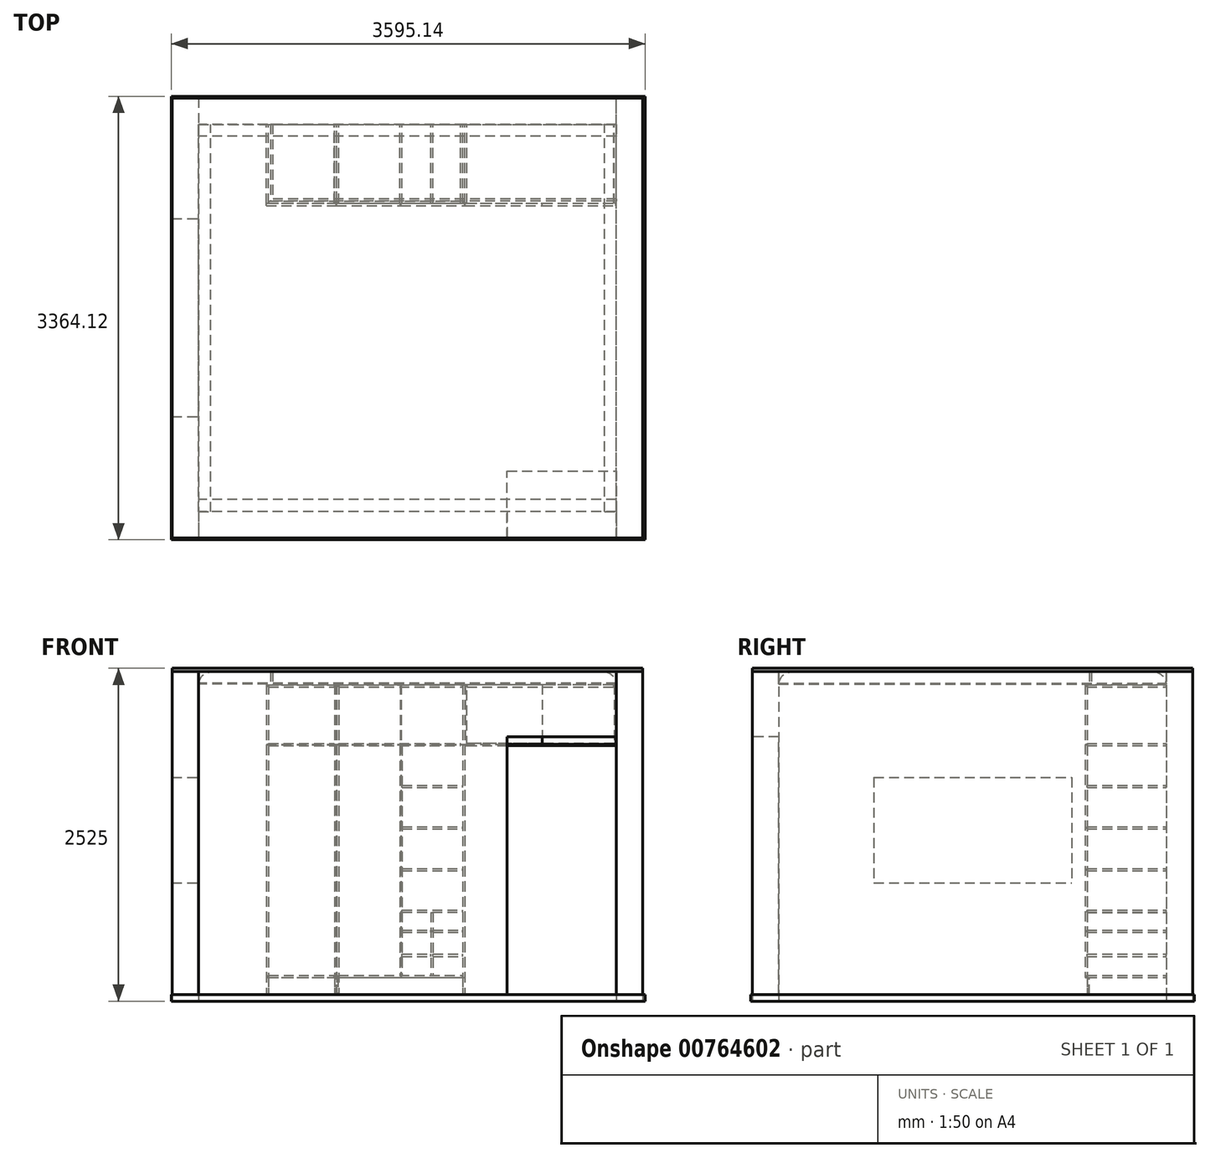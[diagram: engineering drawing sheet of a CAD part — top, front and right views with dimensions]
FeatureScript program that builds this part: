
annotation { "Feature Type Name" : "Feature", "Feature Type Description" : "" }
export const myFeature = defineFeature(function(context is Context, id is Id, definition is map)
    precondition{}
    {
        {
            var Q0;
            Q0=qCreatedBy(makeId("Top.planeOp"),FACE);
            var sketch = newSketch(context, id + "F0", { "sketchPlane" : qUnion([Q0])});
            skLineSegment(sketch, "E0.0.0", {"start": v(-1555, 1015.23) * mm, "end": v(1615, 1015.23) * mm});
            skLineSegment(sketch, "E0.0.1", {"start": v(1615, 1015.23) * mm, "end": v(1615, 1215.23) * mm});
            skLineSegment(sketch, "E0.0.2", {"start": v(1615, 1215.23) * mm, "end": v(-1555, 1215.23) * mm});
            skLineSegment(sketch, "E0.0.3", {"start": v(-1555, 1215.23) * mm, "end": v(-1555, 1015.23) * mm});
            skLineSegment(sketch, "E1.bottom", {"start": v(1815, 1215.23) * mm, "end": v(1615, 1215.23) * mm});
            skLineSegment(sketch, "E1.top", {"start": v(1815, -2124.77) * mm, "end": v(1615, -2124.77) * mm});
            skLineSegment(sketch, "E1.left", {"start": v(1815, 1215.23) * mm, "end": v(1815, -2124.77) * mm});
            skLineSegment(sketch, "E1.right", {"start": v(1615, 1215.23) * mm, "end": v(1615, -2124.77) * mm});
            skLineSegment(sketch, "E2.bottom", {"start": v(-1555, 1215.23) * mm, "end": v(-1755, 1215.23) * mm});
            skLineSegment(sketch, "E2.top", {"start": v(-1555, -2124.77) * mm, "end": v(-1755, -2124.77) * mm});
            skLineSegment(sketch, "E2.left", {"start": v(-1555, 1215.23) * mm, "end": v(-1555, -2124.77) * mm});
            skLineSegment(sketch, "E2.right", {"start": v(-1755, 1215.23) * mm, "end": v(-1755, -2124.77) * mm});
            skLineSegment(sketch, "E3.0.0", {"start": v(-1555, -2124.77) * mm, "end": v(1613.37, -2124.77) * mm});
            skLineSegment(sketch, "E3.0.1", {"start": v(1613.37, -2124.77) * mm, "end": v(1613.37, -1924.77) * mm});
            skLineSegment(sketch, "E3.0.2", {"start": v(1613.37, -1924.77) * mm, "end": v(-1555, -1924.77) * mm});
            skLineSegment(sketch, "E3.0.3", {"start": v(-1555, -1924.77) * mm, "end": v(-1555, -2124.77) * mm});
            skSolve(sketch);
        }
        {
            var Q0;
            {var subQ2=sQuery(id+"F0.wireOp",EDGE,"E1.bottom");Q0=makeQuery(id+"F0.imprint","IMPRINT",FACE,{"disambiguationData":[TD([[makeQuery(id+"F0.imprint","IMPRINT",EDGE,{"derivedFrom":subQ2}),1.0]])]});}
            var Q1;
            {var subQ5=sQuery(id+"F0.wireOp",EDGE,"E2.bottom");Q1=makeQuery(id+"F0.imprint","IMPRINT",FACE,{"disambiguationData":[TD([[makeQuery(id+"F0.imprint","IMPRINT",EDGE,{"derivedFrom":subQ5}),1.0]])]});}
            extrude(context, id + "F1", {"entities" : qUnion([Q0, Q1]), "depth" : 2500 * mm, "offsetDistance" : 25 * mm});
        }
        {
            var Q0;
            {var subQ0=sQuery(id+"F0.wireOp",EDGE,"E0.0.0");Q0=makeQuery(id+"F0.imprint","IMPRINT",FACE,{"disambiguationData":[TD([[makeQuery(id+"F0.imprint","IMPRINT",EDGE,{"derivedFrom":subQ0}),1.0]])]});}
            var Q1;
            Q1=makeQuery(id+"F0.imprint","IMPRINT",FACE,{"disambiguationData":[TD([[makeQuery(id+"F0.imprint","IMPRINT",EDGE,{"derivedFrom":sQuery(id+"F0.wireOp",EDGE,"E3.0.0")}),1.0]])]});
            extrude(context, id + "F2", {"entities" : qUnion([Q0, Q1]), "depth" : 2500 * mm, "offsetDistance" : 25 * mm});
        }
        {
            var Q0;
            Q0=makeQuery(id+"F1.opExtrude","SWEPT_FACE",FACE,{"disambiguationData":[OSD([sQuery(id+"F0.wireOp",EDGE,"E2.left"),sQuery(id+"F0.wireOp",EDGE,"E3.0.3")])]});
            var sketch = newSketch(context, id + "F3", { "sketchPlane" : qUnion([Q0])});
            skLineSegment(sketch, "E4.bottom", {"start": v(-1202.13, 1697) * mm, "end": v(297.87, 1697) * mm});
            skLineSegment(sketch, "E4.top", {"start": v(-1202.13, 897) * mm, "end": v(297.87, 897) * mm});
            skLineSegment(sketch, "E4.left", {"start": v(-1202.13, 1697) * mm, "end": v(-1202.13, 897) * mm});
            skLineSegment(sketch, "E4.right", {"start": v(297.87, 1697) * mm, "end": v(297.87, 897) * mm});
            skSolve(sketch);
        }
        {
            var Q0;
            Q0=makeQuery(id+"F3.imprint","IMPRINT",FACE,{"disambiguationData":[TD([[makeQuery(id+"F3.imprint","IMPRINT",EDGE,{"derivedFrom":sQuery(id+"F3.wireOp",EDGE,"E4.bottom")}),-1.0]])]});
            extrude(context, id + "F4", {"entities" : qUnion([Q0]), "operationType" : NewBodyOperationType.REMOVE, "oppositeDirection" : true, "depth" : 620 * mm, "offsetDistance" : 25 * mm});
        }
        {
            var Q0;
            {var subQ0=sQuery(id+"F0.wireOp",EDGE,"E0.0.0");Q0=makeQuery(id+"F0.imprint","IMPRINT",FACE,{"disambiguationData":[TD([[makeQuery(id+"F0.imprint","IMPRINT",EDGE,{"derivedFrom":subQ0}),1.0]])]});}
            var sketch = newSketch(context, id + "F5", { "sketchPlane" : qUnion([Q0])});
            skLineSegment(sketch, "E5.bottom", {"start": v(-1761.66, -2136.75) * mm, "end": v(1833.48, -2136.75) * mm});
            skLineSegment(sketch, "E5.top", {"start": v(-1761.66, 1227.37) * mm, "end": v(1833.48, 1227.37) * mm});
            skLineSegment(sketch, "E5.left", {"start": v(-1761.66, -2136.75) * mm, "end": v(-1761.66, 1227.37) * mm});
            skLineSegment(sketch, "E5.right", {"start": v(1833.48, -2136.75) * mm, "end": v(1833.48, 1227.37) * mm});
            skSolve(sketch);
        }
        {
            var Q0;
            Q0=makeQuery(id+"F5.imprint","IMPRINT",FACE,{"disambiguationData":[TD([[makeQuery(id+"F5.imprint","IMPRINT",EDGE,{"derivedFrom":sQuery(id+"F5.wireOp",EDGE,"E5.bottom")}),1.0]])]});
            extrude(context, id + "F6", {"entities" : qUnion([Q0]), "depth" : 50 * mm, "offsetDistance" : 25 * mm});
        }
        {
            var Q0;
            Q0=makeQuery(id+"F2.opExtrude","SWEPT_FACE",FACE,{"disambiguationData":[OSD([sQuery(id+"F0.wireOp",EDGE,"E0.0.0")])]});
            var sketch = newSketch(context, id + "F7", { "sketchPlane" : qUnion([Q0])});
            skLineSegment(sketch, "E6.bottom", {"start": v(-1555, 2500) * mm, "end": v(-1462.64, 2500) * mm});
            skLineSegment(sketch, "E6.left", {"start": v(-1555, 2500) * mm, "end": v(-1555, 2412.32) * mm});
            skFitSpline(sketch, "E7", {"points": [v(-1555, 2400.43) * mm, v(-1455, 2500) * mm], "startDerivative": vector(33.84, 289.83) * mm, "endDerivative": vector(27.08, 13.3) * mm});
            skArc(sketch, "E8.filletArc", {"start": v(-1555, 2412.32) * mm, "mid": v(-1554.18, 2411.42) * mm, "end": v(-1553.22, 2412.15) * mm});
            skArc(sketch, "E9.filletArc", {"start": v(-1462.48, 2498.21) * mm, "mid": v(-1461.75, 2499.18) * mm, "end": v(-1462.64, 2500) * mm});
            skLineSegment(sketch, "E10.bottom", {"start": v(1615, 2500) * mm, "end": v(1615, 2407.64) * mm});
            skLineSegment(sketch, "E10.left", {"start": v(1615, 2500) * mm, "end": v(1527.32, 2500) * mm});
            skFitSpline(sketch, "E11", {"points": [v(1515.43, 2500) * mm, v(1615, 2400) * mm], "startDerivative": vector(289.83, -33.84) * mm, "endDerivative": vector(13.3, -27.08) * mm});
            skArc(sketch, "E12.filletArc", {"start": v(1527.32, 2500) * mm, "mid": v(1526.42, 2499.18) * mm, "end": v(1527.15, 2498.22) * mm});
            skArc(sketch, "E13.filletArc", {"start": v(1613.22, 2407.48) * mm, "mid": v(1614.18, 2406.75) * mm, "end": v(1615, 2407.64) * mm});
            skSolve(sketch);
        }
        {
            var Q0;
            Q0=qSketchRegion(id+"F7",true);
            extrude(context, id + "F8", {"entities" : qUnion([Q0]), "depth" : 2940 * mm, "offsetDistance" : 25 * mm});
        }
        {
            var Q0;
            Q0=makeQuery(id+"F1.opExtrude","SWEPT_FACE",FACE,{"disambiguationData":[OSD([sQuery(id+"F0.wireOp",EDGE,"E2.left"),sQuery(id+"F0.wireOp",EDGE,"E3.0.3")])]});
            var sketch = newSketch(context, id + "F9", { "sketchPlane" : qUnion([Q0])});
            skLineSegment(sketch, "E14.bottom", {"start": v(-1924.58, 2500) * mm, "end": v(-1832.23, 2500) * mm});
            skLineSegment(sketch, "E14.left", {"start": v(-1924.58, 2500) * mm, "end": v(-1924.58, 2412.32) * mm});
            skFitSpline(sketch, "E15", {"points": [v(-1924.58, 2400.43) * mm, v(-1824.58, 2500) * mm], "startDerivative": vector(33.84, 289.83) * mm, "endDerivative": vector(27.08, 13.3) * mm});
            skArc(sketch, "E16.filletArc", {"start": v(-1924.58, 2412.32) * mm, "mid": v(-1923.77, 2411.43) * mm, "end": v(-1922.8, 2412.15) * mm});
            skArc(sketch, "E17.filletArc", {"start": v(-1832.06, 2498.22) * mm, "mid": v(-1831.33, 2499.19) * mm, "end": v(-1832.23, 2500) * mm});
            skLineSegment(sketch, "E18.bottom", {"start": v(1014.88, 2500) * mm, "end": v(1014.88, 2407.64) * mm});
            skLineSegment(sketch, "E18.left", {"start": v(1014.88, 2500) * mm, "end": v(927.2, 2500) * mm});
            skFitSpline(sketch, "E19", {"points": [v(915.3, 2500) * mm, v(1014.88, 2400) * mm], "startDerivative": vector(289.83, -33.84) * mm, "endDerivative": vector(13.3, -27.08) * mm});
            skArc(sketch, "E20.filletArc", {"start": v(927.2, 2500) * mm, "mid": v(926.3, 2499.18) * mm, "end": v(927.03, 2498.22) * mm});
            skArc(sketch, "E21.filletArc", {"start": v(1013.1, 2407.48) * mm, "mid": v(1014.06, 2406.75) * mm, "end": v(1014.88, 2407.64) * mm});
            skSolve(sketch);
        }
        {
            var Q0;
            Q0=qSketchRegion(id+"F9",true);
            extrude(context, id + "F10", {"entities" : qUnion([Q0]), "depth" : 3169.2 * mm, "offsetDistance" : 25 * mm});
        }
        {
            var Q0;
            Q0=makeQuery(id+"F2.opExtrude","SWEPT_FACE",FACE,{"disambiguationData":[OSD([sQuery(id+"F0.wireOp",EDGE,"E3.0.0")])]});
            var sketch = newSketch(context, id + "F11", { "sketchPlane" : qUnion([Q0])});
            skLineSegment(sketch, "E22.bottom", {"start": v(1613.37, 49.92) * mm, "end": v(785.99, 49.92) * mm});
            skLineSegment(sketch, "E22.top", {"start": v(1613.37, 2005.08) * mm, "end": v(785.99, 2005.08) * mm});
            skLineSegment(sketch, "E22.left", {"start": v(1613.37, 49.92) * mm, "end": v(1613.37, 2005.08) * mm});
            skLineSegment(sketch, "E22.right", {"start": v(785.99, 49.92) * mm, "end": v(785.99, 2005.08) * mm});
            skSolve(sketch);
        }
        {
            var Q0;
            Q0=makeQuery(id+"F11.imprint","IMPRINT",FACE,{"disambiguationData":[TD([[makeQuery(id+"F11.imprint","IMPRINT",EDGE,{"derivedFrom":sQuery(id+"F11.wireOp",EDGE,"E22.bottom")}),-1.0]])]});
            extrude(context, id + "F12", {"entities" : qUnion([Q0]), "operationType" : NewBodyOperationType.REMOVE, "oppositeDirection" : true, "depth" : 510 * mm, "offsetDistance" : 25 * mm});
        }
        {
            var Q0;
            Q0=makeQuery(id+"F2.opExtrude","CAP_FACE",FACE,{"disambiguationData":[OSD([sQuery(id+"F0.wireOp",EDGE,"E0.0.0"),sQuery(id+"F0.wireOp",EDGE,"E0.0.2"),sQuery(id+"F0.wireOp",EDGE,"E1.right"),sQuery(id+"F0.wireOp",EDGE,"E2.left")])],"isStart":false});
            var sketch = newSketch(context, id + "F13", { "sketchPlane" : qUnion([Q0])});
            skLineSegment(sketch, "E23.0", {"start": v(1815, 1215.23) * mm, "end": v(-1755, 1215.23) * mm});
            skLineSegment(sketch, "E24.0", {"start": v(1815, 1215.23) * mm, "end": v(1815, -2124.77) * mm});
            skLineSegment(sketch, "E25.0", {"start": v(-1755, -2124.77) * mm, "end": v(1815, -2124.77) * mm});
            skLineSegment(sketch, "E26.0", {"start": v(-1755, 1215.23) * mm, "end": v(-1755, -2124.77) * mm});
            skSolve(sketch);
        }
        {
            var Q0;
            Q0=qSketchRegion(id+"F13",true);
            extrude(context, id + "F14", {"entities" : qUnion([Q0]), "depth" : 25 * mm, "offsetDistance" : 25 * mm});
        }
        {
            var Q0;
            Q0=makeQuery(id+"F2.opExtrude","SWEPT_FACE",FACE,{"disambiguationData":[OSD([sQuery(id+"F0.wireOp",EDGE,"E0.0.0")])]});
            var sketch = newSketch(context, id + "F15", { "sketchPlane" : qUnion([Q0])});
            skLineSegment(sketch, "E27", {"start": v(498.7, 98.2) * mm, "end": v(1598.7, 98.2) * mm});
            skLineSegment(sketch, "E28", {"start": v(-930.04, 98.4) * mm, "end": v(469.96, 98.4) * mm});
            skLineSegment(sketch, "E29", {"start": v(-930.56, 51.34) * mm, "end": v(-930.04, 1954.15) * mm});
            skLineSegment(sketch, "E30", {"start": v(-930.04, 1954.15) * mm, "end": v(-930.04, 2500) * mm});
            skSolve(sketch);
        }
        {
            var Q0;
            {var subQ0=sQuery(id+"F0.wireOp",EDGE,"E0.0.0");Q0=makeQuery(id+"F15.imprint","IMPRINT",FACE,{"disambiguationData":[TD([[makeQuery(id+"F15.imprint","IMPRINT",EDGE,{"derivedFrom":makeQuery(id+"F2.opExtrude","CAP_EDGE",EDGE,{"disambiguationData":[OSD([subQ0])],"isStart":true})}),1.0]])]});}
            var sketch = newSketch(context, id + "F16", { "sketchPlane" : qUnion([Q0])});
            skLineSegment(sketch, "E31.bottom", {"start": v(-1039.66, 2400.3) * mm, "end": v(-1023.66, 2400.3) * mm});
            skLineSegment(sketch, "E31.top", {"start": v(-1039.66, 50.3) * mm, "end": v(-1023.66, 50.3) * mm});
            skLineSegment(sketch, "E31.left", {"start": v(-1039.66, 2400.3) * mm, "end": v(-1039.66, 50.3) * mm});
            skLineSegment(sketch, "E31.right", {"start": v(-1023.66, 2400.3) * mm, "end": v(-1023.66, 50.3) * mm});
            skLineSegment(sketch, "E32.bottom", {"start": v(450, 2400.3) * mm, "end": v(466, 2400.3) * mm});
            skLineSegment(sketch, "E32.top", {"start": v(450, 50.3) * mm, "end": v(466, 50.3) * mm});
            skLineSegment(sketch, "E32.left", {"start": v(450, 2400.3) * mm, "end": v(450, 50.3) * mm});
            skLineSegment(sketch, "E32.right", {"start": v(466, 2400.3) * mm, "end": v(466, 50.3) * mm});
            skLineSegment(sketch, "E33.bottom", {"start": v(-1023.54, 1937.99) * mm, "end": v(-1023.54, 1953.99) * mm});
            skLineSegment(sketch, "E33.top", {"start": v(-524.4, 1937.99) * mm, "end": v(-524.4, 1953.99) * mm});
            skLineSegment(sketch, "E33.left", {"start": v(-1023.54, 1937.99) * mm, "end": v(-524.4, 1937.99) * mm});
            skLineSegment(sketch, "E33.right", {"start": v(-1023.54, 1953.99) * mm, "end": v(-524.4, 1953.99) * mm});
            skLineSegment(sketch, "E34.bottom", {"start": v(-1023.33, 2384.28) * mm, "end": v(-1023.33, 2400.28) * mm});
            skLineSegment(sketch, "E34.top", {"start": v(-524.01, 2384.28) * mm, "end": v(-524.01, 2400.28) * mm});
            skLineSegment(sketch, "E34.left", {"start": v(-1023.33, 2384.28) * mm, "end": v(-524.01, 2384.28) * mm});
            skLineSegment(sketch, "E34.right", {"start": v(-1023.33, 2400.28) * mm, "end": v(-524.01, 2400.28) * mm});
            skLineSegment(sketch, "E35.bottom", {"start": v(-1023.48, 180.4) * mm, "end": v(-1023.48, 196.4) * mm});
            skLineSegment(sketch, "E35.top", {"start": v(-524.51, 180.4) * mm, "end": v(-524.51, 196.4) * mm});
            skLineSegment(sketch, "E35.left", {"start": v(-1023.48, 180.4) * mm, "end": v(-524.51, 180.4) * mm});
            skLineSegment(sketch, "E35.right", {"start": v(-1023.48, 196.4) * mm, "end": v(-524.51, 196.4) * mm});
            skLineSegment(sketch, "E36.bottom", {"start": v(-523.66, 2400.3) * mm, "end": v(-507.66, 2400.3) * mm});
            skLineSegment(sketch, "E36.top", {"start": v(-523.66, 50.3) * mm, "end": v(-507.66, 50.3) * mm});
            skLineSegment(sketch, "E36.left", {"start": v(-523.66, 2400.3) * mm, "end": v(-523.66, 50.3) * mm});
            skLineSegment(sketch, "E36.right", {"start": v(-507.66, 2400.3) * mm, "end": v(-507.66, 50.3) * mm});
            skLineSegment(sketch, "E37.bottom", {"start": v(-28.8, 1937.8) * mm, "end": v(-12.8, 1937.8) * mm});
            skLineSegment(sketch, "E37.top", {"start": v(-28.8, 196.92) * mm, "end": v(-12.8, 196.92) * mm});
            skLineSegment(sketch, "E37.left", {"start": v(-28.8, 1937.8) * mm, "end": v(-28.8, 196.92) * mm});
            skLineSegment(sketch, "E37.right", {"start": v(-12.8, 1937.8) * mm, "end": v(-12.8, 196.92) * mm});
            skLineSegment(sketch, "E38.bottom", {"start": v(-491.17, 2384.3) * mm, "end": v(-491.17, 2400.3) * mm});
            skLineSegment(sketch, "E38.top", {"start": v(449.95, 2384.3) * mm, "end": v(449.95, 2400.3) * mm});
            skLineSegment(sketch, "E38.left", {"start": v(-491.17, 2384.3) * mm, "end": v(449.95, 2384.3) * mm});
            skLineSegment(sketch, "E38.right", {"start": v(-491.17, 2400.3) * mm, "end": v(449.95, 2400.3) * mm});
            skLineSegment(sketch, "E39.bottom", {"start": v(-491.28, 1937.98) * mm, "end": v(-491.28, 1953.98) * mm});
            skLineSegment(sketch, "E39.top", {"start": v(433.7, 1937.98) * mm, "end": v(433.7, 1953.98) * mm});
            skLineSegment(sketch, "E39.left", {"start": v(-491.28, 1937.98) * mm, "end": v(433.7, 1937.98) * mm});
            skLineSegment(sketch, "E39.right", {"start": v(-491.28, 1953.98) * mm, "end": v(433.7, 1953.98) * mm});
            skLineSegment(sketch, "E40.bottom", {"start": v(-491.2, 180.4) * mm, "end": v(-491.2, 196.4) * mm});
            skLineSegment(sketch, "E40.top", {"start": v(449.77, 180.4) * mm, "end": v(449.77, 196.4) * mm});
            skLineSegment(sketch, "E40.left", {"start": v(-491.2, 180.4) * mm, "end": v(449.77, 180.4) * mm});
            skLineSegment(sketch, "E40.right", {"start": v(-491.2, 196.4) * mm, "end": v(449.77, 196.4) * mm});
            skPoint(sketch, "E41", {"position": v(-28.8, 1937.98) * mm});
            skLineSegment(sketch, "E42.bottom", {"start": v(-11.33, 1621.98) * mm, "end": v(-11.33, 1637.98) * mm});
            skLineSegment(sketch, "E42.top", {"start": v(449.6, 1621.98) * mm, "end": v(449.6, 1637.98) * mm});
            skLineSegment(sketch, "E42.left", {"start": v(-11.33, 1621.98) * mm, "end": v(449.6, 1621.98) * mm});
            skLineSegment(sketch, "E42.right", {"start": v(-11.33, 1637.98) * mm, "end": v(449.6, 1637.98) * mm});
            skLineSegment(sketch, "E43.bottom", {"start": v(-11.33, 1305.98) * mm, "end": v(-11.33, 1321.98) * mm});
            skLineSegment(sketch, "E43.top", {"start": v(449.6, 1305.98) * mm, "end": v(449.6, 1321.98) * mm});
            skLineSegment(sketch, "E43.left", {"start": v(-11.33, 1305.98) * mm, "end": v(449.6, 1305.98) * mm});
            skLineSegment(sketch, "E43.right", {"start": v(-11.33, 1321.98) * mm, "end": v(449.6, 1321.98) * mm});
            skLineSegment(sketch, "E44.bottom", {"start": v(-11.33, 989.98) * mm, "end": v(-11.33, 1005.98) * mm});
            skLineSegment(sketch, "E44.top", {"start": v(449.6, 989.98) * mm, "end": v(449.6, 1005.98) * mm});
            skLineSegment(sketch, "E44.left", {"start": v(-11.33, 989.98) * mm, "end": v(449.6, 989.98) * mm});
            skLineSegment(sketch, "E44.right", {"start": v(-11.33, 1005.98) * mm, "end": v(449.6, 1005.98) * mm});
            skLineSegment(sketch, "E45.bottom", {"start": v(-11.33, 673.98) * mm, "end": v(-11.33, 689.98) * mm});
            skLineSegment(sketch, "E45.top", {"start": v(449.6, 673.98) * mm, "end": v(449.6, 689.98) * mm});
            skLineSegment(sketch, "E45.left", {"start": v(-11.33, 673.98) * mm, "end": v(449.6, 673.98) * mm});
            skLineSegment(sketch, "E45.right", {"start": v(-11.33, 689.98) * mm, "end": v(449.6, 689.98) * mm});
            skLineSegment(sketch, "E46.top", {"start": v(207.2, 196.51) * mm, "end": v(223.2, 196.51) * mm});
            skLineSegment(sketch, "E46.left", {"start": v(207.2, 672.57) * mm, "end": v(207.2, 196.51) * mm});
            skLineSegment(sketch, "E46.right", {"start": v(223.2, 672.57) * mm, "end": v(223.2, 196.51) * mm});
            skLineSegment(sketch, "E47", {"start": v(207.2, 672.57) * mm, "end": v(223.2, 672.57) * mm});
            skLineSegment(sketch, "E48.bottom", {"start": v(-11.33, 523.98) * mm, "end": v(-11.33, 539.98) * mm});
            skLineSegment(sketch, "E48.top", {"start": v(206.59, 523.98) * mm, "end": v(206.59, 539.98) * mm});
            skLineSegment(sketch, "E48.left", {"start": v(-11.33, 523.98) * mm, "end": v(206.59, 523.98) * mm});
            skLineSegment(sketch, "E48.right", {"start": v(-11.33, 539.98) * mm, "end": v(206.59, 539.98) * mm});
            skLineSegment(sketch, "E49.bottom", {"start": v(-11.33, 339.98) * mm, "end": v(-11.33, 355.98) * mm});
            skLineSegment(sketch, "E49.top", {"start": v(206.59, 339.98) * mm, "end": v(206.59, 355.98) * mm});
            skLineSegment(sketch, "E49.left", {"start": v(-11.33, 339.98) * mm, "end": v(206.59, 339.98) * mm});
            skLineSegment(sketch, "E49.right", {"start": v(-11.33, 355.98) * mm, "end": v(206.59, 355.98) * mm});
            skLineSegment(sketch, "E50.bottom", {"start": v(223.6, 523.98) * mm, "end": v(223.6, 539.98) * mm});
            skLineSegment(sketch, "E50.top", {"start": v(449.5, 523.98) * mm, "end": v(449.5, 539.98) * mm});
            skLineSegment(sketch, "E50.left", {"start": v(223.6, 523.98) * mm, "end": v(449.5, 523.98) * mm});
            skLineSegment(sketch, "E50.right", {"start": v(223.6, 539.98) * mm, "end": v(449.5, 539.98) * mm});
            skLineSegment(sketch, "E51.bottom", {"start": v(223.6, 339.98) * mm, "end": v(223.6, 355.98) * mm});
            skLineSegment(sketch, "E51.top", {"start": v(449.82, 339.98) * mm, "end": v(449.82, 355.98) * mm});
            skLineSegment(sketch, "E51.left", {"start": v(223.6, 339.98) * mm, "end": v(449.82, 339.98) * mm});
            skLineSegment(sketch, "E51.right", {"start": v(223.6, 355.98) * mm, "end": v(449.82, 355.98) * mm});
            skLineSegment(sketch, "E52.bottom", {"start": v(-507.52, 2400.3) * mm, "end": v(-491.52, 2400.3) * mm});
            skLineSegment(sketch, "E52.top", {"start": v(-507.52, 50.3) * mm, "end": v(-491.52, 50.3) * mm});
            skLineSegment(sketch, "E52.left", {"start": v(-507.52, 2400.3) * mm, "end": v(-507.52, 50.3) * mm});
            skLineSegment(sketch, "E52.right", {"start": v(-491.52, 2400.3) * mm, "end": v(-491.52, 50.3) * mm});
            skSolve(sketch);
        }
        {
            var Q0;
            Q0=makeQuery(id+"F16.imprint","IMPRINT",FACE,{"disambiguationData":[TD([[makeQuery(id+"F16.imprint","IMPRINT",EDGE,{"derivedFrom":sQuery(id+"F16.wireOp",EDGE,"E32.bottom")}),-1.0]])]});
            var Q1;
            {var subQ1=sQuery(id+"F16.wireOp",EDGE,"E31.bottom");Q1=makeQuery(id+"F16.imprint","IMPRINT",FACE,{"disambiguationData":[TD([[makeQuery(id+"F16.imprint","IMPRINT",EDGE,{"derivedFrom":subQ1}),-1.0]])]});}
            var Q2;
            Q2=makeQuery(id+"F16.imprint","IMPRINT",FACE,{"disambiguationData":[TD([[makeQuery(id+"F16.imprint","IMPRINT",EDGE,{"derivedFrom":sQuery(id+"F16.wireOp",EDGE,"E34.bottom")}),-1.0]])]});
            var Q3;
            Q3=makeQuery(id+"F16.imprint","IMPRINT",FACE,{"disambiguationData":[TD([[makeQuery(id+"F16.imprint","IMPRINT",EDGE,{"derivedFrom":sQuery(id+"F16.wireOp",EDGE,"E36.bottom")}),-1.0]])]});
            var Q4;
            Q4=makeQuery(id+"F16.imprint","IMPRINT",FACE,{"disambiguationData":[TD([[makeQuery(id+"F16.imprint","IMPRINT",EDGE,{"derivedFrom":sQuery(id+"F16.wireOp",EDGE,"E35.bottom")}),-1.0]])]});
            var Q5;
            Q5=makeQuery(id+"F16.imprint","IMPRINT",FACE,{"disambiguationData":[TD([[makeQuery(id+"F16.imprint","IMPRINT",EDGE,{"derivedFrom":sQuery(id+"F16.wireOp",EDGE,"E38.bottom")}),-1.0]])]});
            var Q6;
            Q6=makeQuery(id+"F16.imprint","IMPRINT",FACE,{"disambiguationData":[TD([[makeQuery(id+"F16.imprint","IMPRINT",EDGE,{"derivedFrom":sQuery(id+"F16.wireOp",EDGE,"E40.bottom")}),-1.0]])]});
            var Q7;
            Q7=makeQuery(id+"F16.imprint","IMPRINT",FACE,{"disambiguationData":[TD([[makeQuery(id+"F16.imprint","IMPRINT",EDGE,{"derivedFrom":sQuery(id+"F16.wireOp",EDGE,"E37.bottom")}),-1.0]])]});
            var Q8;
            Q8=makeQuery(id+"F16.imprint","IMPRINT",FACE,{"disambiguationData":[TD([[makeQuery(id+"F16.imprint","IMPRINT",EDGE,{"derivedFrom":sQuery(id+"F16.wireOp",EDGE,"E52.bottom")}),-1.0]])]});
            extrude(context, id + "F17", {"entities" : qUnion([Q0, Q1, Q2, Q3, Q4, Q5, Q6, Q7, Q8]), "depth" : 600 * mm, "offsetDistance" : 25 * mm});
        }
        {
            var Q0;
            Q0=makeQuery(id+"F16.imprint","IMPRINT",FACE,{"disambiguationData":[TD([[makeQuery(id+"F16.imprint","IMPRINT",EDGE,{"derivedFrom":sQuery(id+"F16.wireOp",EDGE,"E33.bottom")}),-1.0]])]});
            var Q1;
            Q1=makeQuery(id+"F16.imprint","IMPRINT",FACE,{"disambiguationData":[TD([[makeQuery(id+"F16.imprint","IMPRINT",EDGE,{"derivedFrom":sQuery(id+"F16.wireOp",EDGE,"E39.bottom")}),-1.0]])]});
            var Q2;
            Q2=makeQuery(id+"F16.imprint","IMPRINT",FACE,{"disambiguationData":[TD([[makeQuery(id+"F16.imprint","IMPRINT",EDGE,{"derivedFrom":sQuery(id+"F16.wireOp",EDGE,"E42.bottom")}),-1.0]])]});
            var Q3;
            Q3=makeQuery(id+"F16.imprint","IMPRINT",FACE,{"disambiguationData":[TD([[makeQuery(id+"F16.imprint","IMPRINT",EDGE,{"derivedFrom":sQuery(id+"F16.wireOp",EDGE,"E43.bottom")}),-1.0]])]});
            var Q4;
            Q4=makeQuery(id+"F16.imprint","IMPRINT",FACE,{"disambiguationData":[TD([[makeQuery(id+"F16.imprint","IMPRINT",EDGE,{"derivedFrom":sQuery(id+"F16.wireOp",EDGE,"E44.bottom")}),-1.0]])]});
            var Q5;
            Q5=makeQuery(id+"F16.imprint","IMPRINT",FACE,{"disambiguationData":[TD([[makeQuery(id+"F16.imprint","IMPRINT",EDGE,{"derivedFrom":sQuery(id+"F16.wireOp",EDGE,"E45.bottom")}),-1.0]])]});
            var Q6;
            Q6=makeQuery(id+"F16.imprint","IMPRINT",FACE,{"disambiguationData":[TD([[makeQuery(id+"F16.imprint","IMPRINT",EDGE,{"derivedFrom":sQuery(id+"F16.wireOp",EDGE,"E46.top")}),1.0]])]});
            var Q7;
            Q7=makeQuery(id+"F16.imprint","IMPRINT",FACE,{"disambiguationData":[TD([[makeQuery(id+"F16.imprint","IMPRINT",EDGE,{"derivedFrom":sQuery(id+"F16.wireOp",EDGE,"E48.bottom")}),-1.0]])]});
            var Q8;
            Q8=makeQuery(id+"F16.imprint","IMPRINT",FACE,{"disambiguationData":[TD([[makeQuery(id+"F16.imprint","IMPRINT",EDGE,{"derivedFrom":sQuery(id+"F16.wireOp",EDGE,"E49.bottom")}),-1.0]])]});
            var Q9;
            Q9=makeQuery(id+"F16.imprint","IMPRINT",FACE,{"disambiguationData":[TD([[makeQuery(id+"F16.imprint","IMPRINT",EDGE,{"derivedFrom":sQuery(id+"F16.wireOp",EDGE,"E50.bottom")}),-1.0]])]});
            var Q10;
            Q10=makeQuery(id+"F16.imprint","IMPRINT",FACE,{"disambiguationData":[TD([[makeQuery(id+"F16.imprint","IMPRINT",EDGE,{"derivedFrom":sQuery(id+"F16.wireOp",EDGE,"E51.bottom")}),-1.0]])]});
            extrude(context, id + "F18", {"entities" : qUnion([Q0, Q1, Q2, Q3, Q4, Q5, Q6, Q7, Q8, Q9, Q10]), "depth" : 600 * mm, "offsetDistance" : 25 * mm});
        }
        {
            var Q0;
            Q0=makeQuery(id+"F16.imprint","IMPRINT",FACE,{"disambiguationData":[TD([[makeQuery(id+"F16.imprint","IMPRINT",EDGE,{"derivedFrom":sQuery(id+"F16.wireOp",EDGE,"E31.bottom")}),1.0]])]});
            var sketch = newSketch(context, id + "F19", { "sketchPlane" : qUnion([Q0])});
            skLineSegment(sketch, "E53.0.0", {"start": v(482.33, 2384.3) * mm, "end": v(1596.28, 2384.3) * mm});
            skLineSegment(sketch, "E53.0.1", {"start": v(1596.28, 2384.3) * mm, "end": v(1596.28, 2400.3) * mm});
            skLineSegment(sketch, "E53.0.2", {"start": v(1596.28, 2400.3) * mm, "end": v(482.33, 2400.3) * mm});
            skLineSegment(sketch, "E53.0.3", {"start": v(482.33, 2400.3) * mm, "end": v(482.33, 2384.3) * mm});
            skLineSegment(sketch, "E54.0.0", {"start": v(466.1, 2400.3) * mm, "end": v(466.1, 1937.9) * mm});
            skLineSegment(sketch, "E54.0.1", {"start": v(466.1, 1937.9) * mm, "end": v(482.1, 1937.9) * mm});
            skLineSegment(sketch, "E54.0.2", {"start": v(482.1, 1937.9) * mm, "end": v(482.1, 2400.3) * mm});
            skLineSegment(sketch, "E54.0.3", {"start": v(482.1, 2400.3) * mm, "end": v(466.1, 2400.3) * mm});
            skLineSegment(sketch, "E55.0.0", {"start": v(1597.76, 2400.3) * mm, "end": v(1597.76, 1937.95) * mm});
            skLineSegment(sketch, "E55.0.1", {"start": v(1597.76, 1937.95) * mm, "end": v(1613.76, 1937.95) * mm});
            skLineSegment(sketch, "E55.0.2", {"start": v(1613.76, 1937.95) * mm, "end": v(1613.76, 2400.3) * mm});
            skLineSegment(sketch, "E55.0.3", {"start": v(1613.76, 2400.3) * mm, "end": v(1597.76, 2400.3) * mm});
            skLineSegment(sketch, "E56.0.0", {"start": v(482.28, 1937.98) * mm, "end": v(1597.13, 1937.98) * mm});
            skLineSegment(sketch, "E56.0.1", {"start": v(1597.13, 1937.98) * mm, "end": v(1597.13, 1953.98) * mm});
            skLineSegment(sketch, "E56.0.2", {"start": v(1597.13, 1953.98) * mm, "end": v(482.28, 1953.98) * mm});
            skLineSegment(sketch, "E56.0.3", {"start": v(482.28, 1953.98) * mm, "end": v(482.28, 1937.98) * mm});
            skSolve(sketch);
        }
        {
            var Q0;
            Q0=qSketchRegion(id+"F19",true);
            extrude(context, id + "F20", {"entities" : qUnion([Q0]), "depth" : 600 * mm, "offsetDistance" : 25 * mm});
        }
        {
            var Q0;
            Q0=makeQuery(id+"F17.opExtrude","SWEPT_FACE",FACE,{"disambiguationData":[OSD([sQuery(id+"F16.wireOp",EDGE,"E36.left")])]});
            var sketch = newSketch(context, id + "F21", { "sketchPlane" : qUnion([Q0])});
            skLineSegment(sketch, "E57.bottom", {"start": v(-431.22, 180.59) * mm, "end": v(-415.22, 180.59) * mm});
            skLineSegment(sketch, "E57.top", {"start": v(-431.22, 49.78) * mm, "end": v(-415.22, 49.78) * mm});
            skLineSegment(sketch, "E57.left", {"start": v(-431.22, 180.59) * mm, "end": v(-431.22, 49.78) * mm});
            skLineSegment(sketch, "E57.right", {"start": v(-415.22, 180.59) * mm, "end": v(-415.22, 49.78) * mm});
            skSolve(sketch);
        }
        {
            var Q0;
            {var subQ0=sQuery(id+"F21.wireOp",EDGE,"E57.left");var subQ1=sQuery(id+"F21.wireOp",EDGE,"E57.bottom");var subQ2=makeQuery(id+"F21.imprint","INTERSECT",VERTEX,{"derivedFrom":[subQ1,subQ0]});Q0=makeQuery(id+"F21.imprint","IMPRINT",FACE,{"disambiguationData":[TD([[makeQuery(id+"F21.imprint","IMPRINT",EDGE,{"disambiguationData":[TD([[subQ2,-1.0]])],"derivedFrom":subQ1}),-1.0]])]});}
            extrude(context, id + "F22", {"entities" : qUnion([Q0]), "operationType" : NewBodyOperationType.REMOVE, "oppositeDirection" : true, "depth" : 25 * mm, "offsetDistance" : 25 * mm});
        }
        {
            var Q0;
            {var subQ0=sQuery(id+"F21.wireOp",EDGE,"E57.left");var subQ1=sQuery(id+"F21.wireOp",EDGE,"E57.bottom");var subQ2=makeQuery(id+"F21.imprint","INTERSECT",VERTEX,{"derivedFrom":[subQ1,subQ0]});Q0=makeQuery(id+"F21.imprint","IMPRINT",FACE,{"disambiguationData":[TD([[makeQuery(id+"F21.imprint","IMPRINT",EDGE,{"disambiguationData":[TD([[subQ2,-1.0]])],"derivedFrom":subQ1}),-1.0]])]});}
            extrude(context, id + "F23", {"entities" : qUnion([Q0]), "depth" : 499.9 * mm, "offsetDistance" : 25 * mm, "hasSecondDirection" : true, "secondDirectionOppositeDirection" : true, "secondDirectionDepth" : 974 * mm});
        }
        {
            var Q0;
            Q0=makeQuery(id+"F17.opExtrude","CAP_FACE",FACE,{"disambiguationData":[OSD([sQuery(id+"F16.wireOp",EDGE,"E31.bottom"),sQuery(id+"F16.wireOp",EDGE,"E31.top"),sQuery(id+"F16.wireOp",EDGE,"E31.left"),sQuery(id+"F16.wireOp",EDGE,"E31.right")])],"isStart":false});
            var sketch = newSketch(context, id + "F24", { "sketchPlane" : qUnion([Q0])});
            skLineSegment(sketch, "E58.0", {"start": v(-1039.66, 1945.74) * mm, "end": v(-510.25, 1945.9) * mm});
            skLineSegment(sketch, "E59.0", {"start": v(-1039.66, 180.25) * mm, "end": v(-510.25, 180.58) * mm});
            skLineSegment(sketch, "E60.0", {"start": v(-510.25, 1945.9) * mm, "end": v(-510.25, 180.58) * mm});
            skLineSegment(sketch, "E61.0", {"start": v(-1039.66, 1945.74) * mm, "end": v(-1039.66, 180.25) * mm});
            skLineSegment(sketch, "E62.0", {"start": v(-507.65, 1945.9) * mm, "end": v(-22.65, 1945.89) * mm});
            skLineSegment(sketch, "E63.0", {"start": v(-507.65, 180.6) * mm, "end": v(-22.65, 180.9) * mm});
            skLineSegment(sketch, "E64.0", {"start": v(-22.65, 1945.89) * mm, "end": v(-22.65, 180.9) * mm});
            skLineSegment(sketch, "E65.0", {"start": v(-507.65, 1945.9) * mm, "end": v(-507.65, 180.6) * mm});
            skLineSegment(sketch, "E66.0", {"start": v(-19.04, 1945.87) * mm, "end": v(465.95, 1945.86) * mm});
            skLineSegment(sketch, "E67.0", {"start": v(-19.04, 180.56) * mm, "end": v(465.95, 180.87) * mm});
            skLineSegment(sketch, "E68.0", {"start": v(465.95, 1945.86) * mm, "end": v(465.95, 180.87) * mm});
            skLineSegment(sketch, "E69.0", {"start": v(-19.04, 1945.87) * mm, "end": v(-19.04, 180.56) * mm});
            skLineSegment(sketch, "E70.0", {"start": v(-1039.66, 2400.25) * mm, "end": v(-510.25, 2400.41) * mm});
            skLineSegment(sketch, "E71.0", {"start": v(-1039.66, 1946.94) * mm, "end": v(-510.25, 1947.27) * mm});
            skLineSegment(sketch, "E72.0", {"start": v(-510.25, 2400.41) * mm, "end": v(-510.25, 1947.27) * mm});
            skLineSegment(sketch, "E73.0", {"start": v(-1039.66, 2400.25) * mm, "end": v(-1039.66, 1946.94) * mm});
            skLineSegment(sketch, "E74.0", {"start": v(-507.65, 2400.42) * mm, "end": v(-22.67, 2400.57) * mm});
            skLineSegment(sketch, "E75.0", {"start": v(-507.65, 1947.27) * mm, "end": v(-22.67, 1947.58) * mm});
            skLineSegment(sketch, "E76.0", {"start": v(-22.67, 2400.57) * mm, "end": v(-22.67, 1947.58) * mm});
            skLineSegment(sketch, "E77.0", {"start": v(-507.65, 2400.42) * mm, "end": v(-507.65, 1947.27) * mm});
            skLineSegment(sketch, "E78.0", {"start": v(-19.04, 2400.6) * mm, "end": v(465.93, 2400.75) * mm});
            skLineSegment(sketch, "E79.0", {"start": v(-19.04, 1947.46) * mm, "end": v(465.93, 1947.76) * mm});
            skLineSegment(sketch, "E80.0", {"start": v(465.93, 2400.75) * mm, "end": v(465.93, 1947.76) * mm});
            skLineSegment(sketch, "E81.0", {"start": v(-19.04, 2400.6) * mm, "end": v(-19.04, 1947.46) * mm});
            skLineSegment(sketch, "E82.0", {"start": v(467.65, 2400.9) * mm, "end": v(1051.28, 2401.08) * mm});
            skLineSegment(sketch, "E83.0", {"start": v(467.65, 1947.76) * mm, "end": v(1051.28, 1948.13) * mm});
            skLineSegment(sketch, "E84.0", {"start": v(1051.28, 2401.08) * mm, "end": v(1051.28, 1948.13) * mm});
            skLineSegment(sketch, "E85.0", {"start": v(467.65, 2400.9) * mm, "end": v(467.65, 1947.76) * mm});
            skLineSegment(sketch, "E86.0", {"start": v(1053.2, 2401.12) * mm, "end": v(1612.26, 2401.3) * mm});
            skLineSegment(sketch, "E87.0", {"start": v(1053.2, 1947.95) * mm, "end": v(1612.26, 1948.3) * mm});
            skLineSegment(sketch, "E88.0", {"start": v(1612.26, 2401.3) * mm, "end": v(1612.26, 1948.3) * mm});
            skLineSegment(sketch, "E89.0", {"start": v(1053.2, 2401.12) * mm, "end": v(1053.2, 1947.95) * mm});
            skSolve(sketch);
        }
        {
            var Q0;
            Q0=qSketchRegion(id+"F24",true);
            extrude(context, id + "F25", {"entities" : qUnion([Q0]), "depth" : 16 * mm, "offsetDistance" : 25 * mm});
        }
        {
            var Q0;
            Q0=makeQuery(id+"F17.opExtrude","SWEPT_FACE",FACE,{"disambiguationData":[OSD([sQuery(id+"F16.wireOp",EDGE,"E38.right")])]});
            var sketch = newSketch(context, id + "F26", { "sketchPlane" : qUnion([Q0])});
            skLineSegment(sketch, "E90.top", {"start": v(1614.2, 432.1) * mm, "end": v(-1008.45, 432.1) * mm});
            skLineSegment(sketch, "E90.right", {"start": v(-1008.45, 1015.37) * mm, "end": v(-1008.45, 432.1) * mm});
            skLineSegment(sketch, "E91.0", {"start": v(1614.63, 448.1) * mm, "end": v(-992.45, 448.1) * mm});
            skLineSegment(sketch, "E91.3", {"start": v(-992.45, 1015.37) * mm, "end": v(-992.45, 448.1) * mm});
            skLineSegment(sketch, "E92", {"start": v(-1008.45, 1015.37) * mm, "end": v(-992.45, 1015.37) * mm});
            skLineSegment(sketch, "E93", {"start": v(1614.63, 448.1) * mm, "end": v(1614.2, 432.1) * mm});
            skSolve(sketch);
        }
        {
            var Q0;
            Q0=qSketchRegion(id+"F26",true);
            extrude(context, id + "F27", {"entities" : qUnion([Q0]), "depth" : 100 * mm, "offsetDistance" : 25 * mm});
        }
    });
